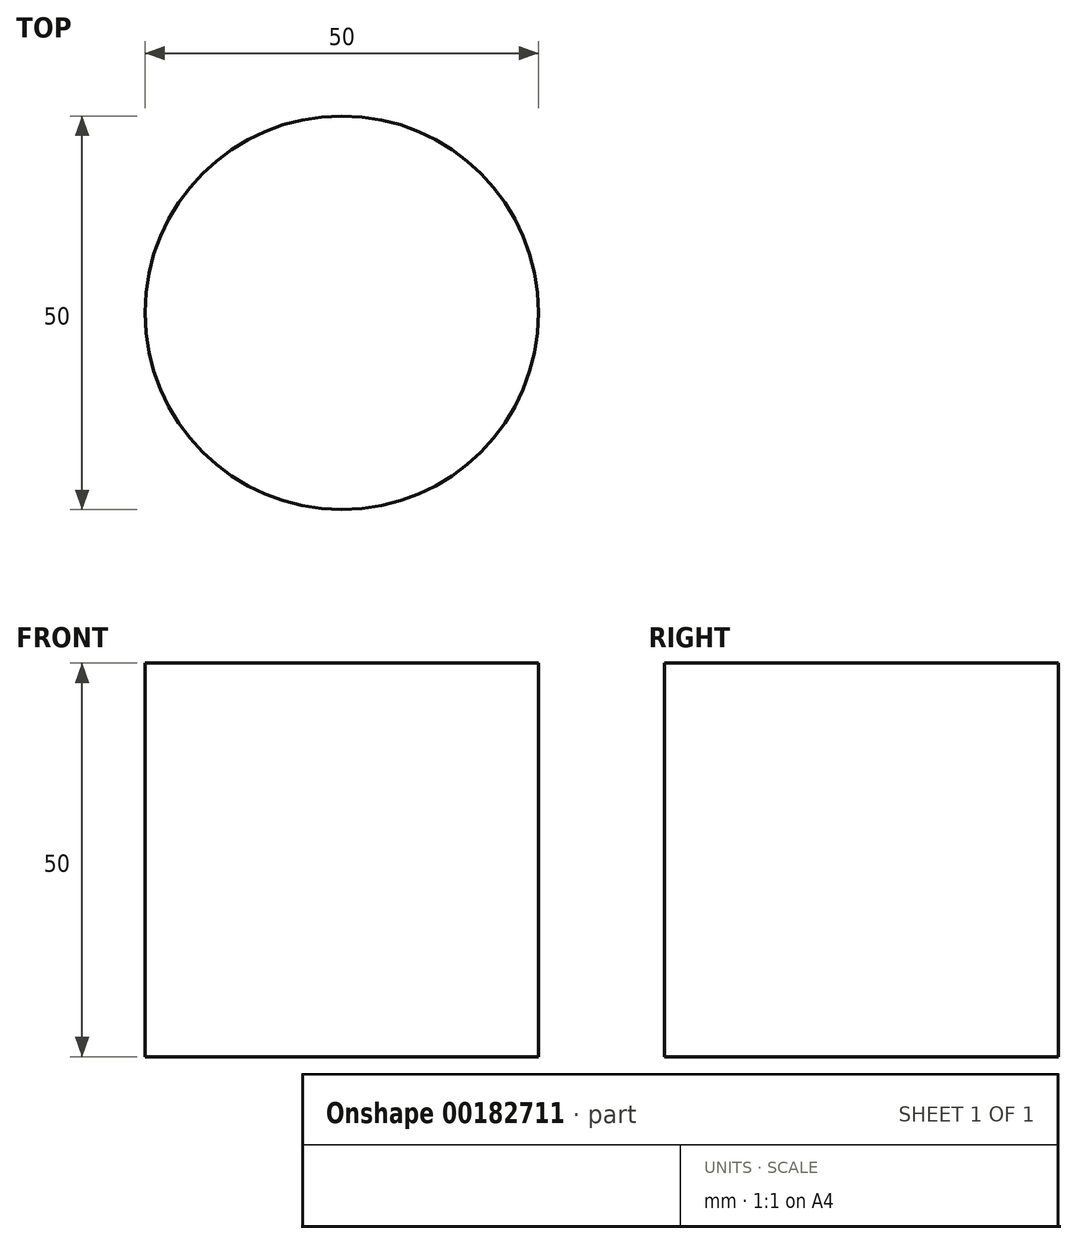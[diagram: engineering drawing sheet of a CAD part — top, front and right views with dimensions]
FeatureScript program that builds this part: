
annotation { "Feature Type Name" : "Feature", "Feature Type Description" : "" }
export const myFeature = defineFeature(function(context is Context, id is Id, definition is map)
    precondition{}
    {
        {
            var Q0;
            Q0=qCreatedBy(makeId("Top.planeOp"),FACE);
            var sketch = newSketch(context, id + "F0", { "sketchPlane" : qUnion([Q0])});
            skCircle(sketch, "E0", {"center": v(0, 0) * mm, "radius": 25 * mm});
            skSolve(sketch);
        }
        {
            var Q0;
            Q0=makeQuery(id+"F0.imprint","IMPRINT",FACE,{"disambiguationData":[TD([[makeQuery(id+"F0.imprint","IMPRINT",EDGE,{"derivedFrom":sQuery(id+"F0.wireOp",EDGE,"E0")}),1.0]])]});
            extrude(context, id + "F1", {"entities" : qUnion([Q0]), "offsetDistance" : 25 * mm, "depth" : 50 * mm});
        }
    });
